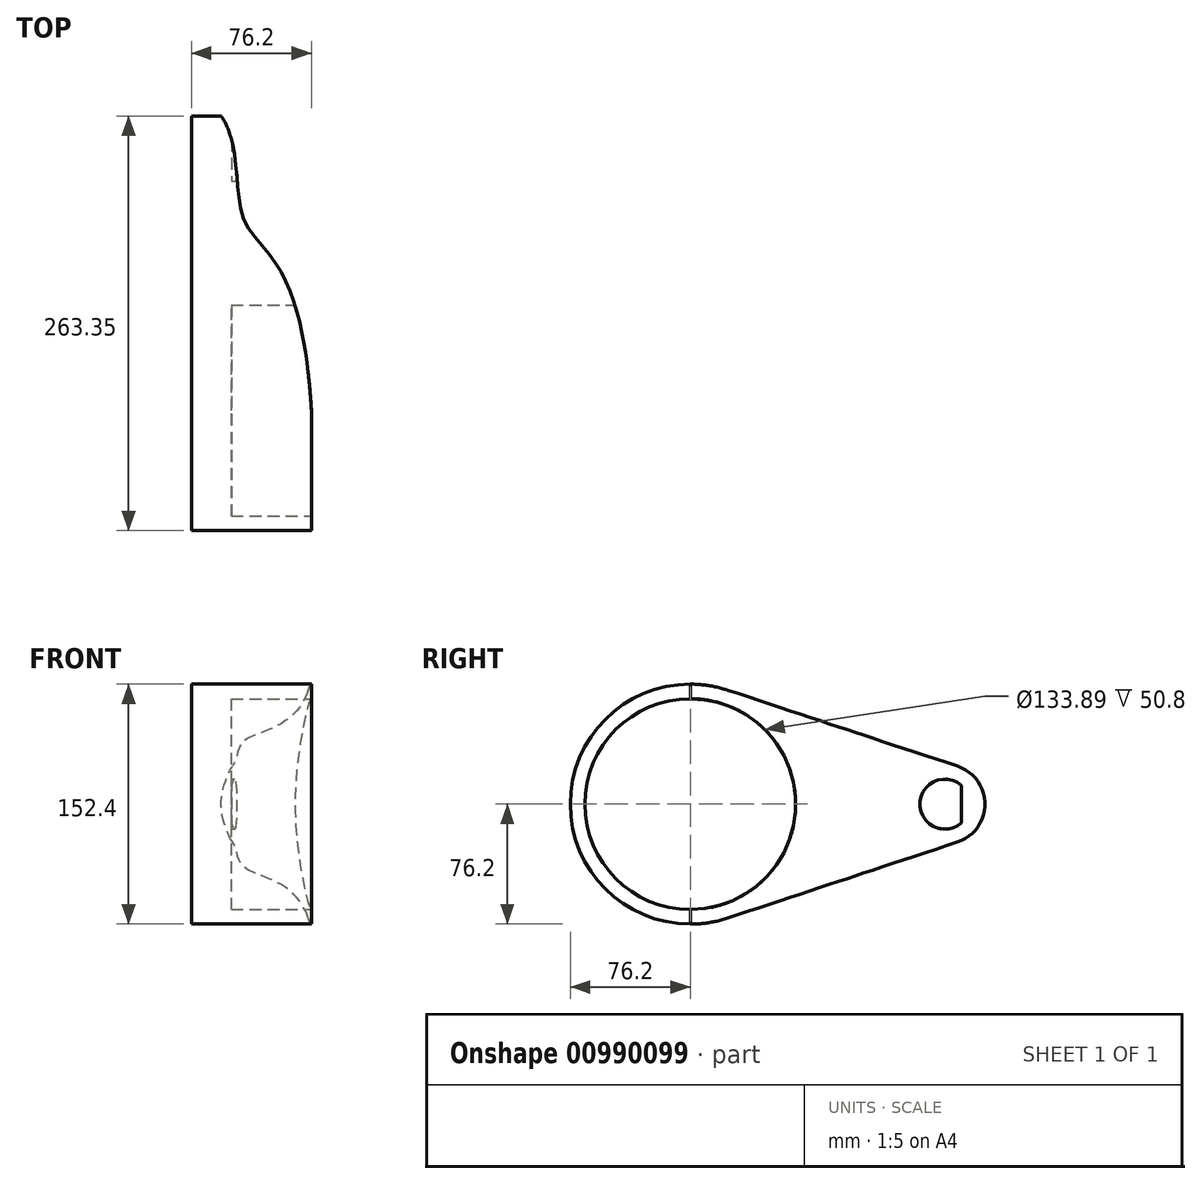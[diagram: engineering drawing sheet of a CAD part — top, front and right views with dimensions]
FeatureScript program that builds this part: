
annotation { "Feature Type Name" : "Feature", "Feature Type Description" : "" }
export const myFeature = defineFeature(function(context is Context, id is Id, definition is map)
    precondition{}
    {
        {
            var Q0;
            Q0=qCreatedBy(makeId("Right.planeOp"),FACE);
            var sketch = newSketch(context, id + "F0", { "sketchPlane" : qUnion([Q0])});
            skArc(sketch, "E0", {"start": v(23.93, 72.34) * mm, "mid": v(-76.2, 0) * mm, "end": v(23.93, -72.34) * mm});
            skArc(sketch, "E1", {"start": v(169.73, -24.11) * mm, "mid": v(187.15, 0) * mm, "end": v(169.73, 24.11) * mm});
            skLineSegment(sketch, "E2", {"start": v(23.93, 72.34) * mm, "end": v(169.73, 24.11) * mm});
            skLineSegment(sketch, "E3", {"start": v(23.93, -72.34) * mm, "end": v(169.73, -24.11) * mm});
            skSolve(sketch);
        }
        {
            var Q0;
            {var subQ0=sQuery(id+"F0.wireOp",EDGE,"E2");Q0=makeQuery(id+"F0.imprint","IMPRINT",FACE,{"disambiguationData":[TD([[makeQuery(id+"F0.imprint","IMPRINT",EDGE,{"derivedFrom":subQ0}),-1.0]])]});}
            var Q1;
            {var subQ0=sQuery(id+"F0.wireOp",EDGE,"E0");var subQ1=makeQuery(id+"F0.imprint","INTERSECT",VERTEX,{"derivedFrom":[subQ0,sQuery(id+"F0.wireOp",EDGE,"E2")]});Q1=makeQuery(id+"F0.imprint","IMPRINT",FACE,{"disambiguationData":[TD([[makeQuery(id+"F0.imprint","IMPRINT",EDGE,{"disambiguationData":[TD([[subQ1,-1.0]])],"derivedFrom":subQ0}),1.0]])]});}
            var Q2;
            {var subQ0=sQuery(id+"F0.wireOp",EDGE,"E1");var subQ1=makeQuery(id+"F0.imprint","INTERSECT",VERTEX,{"derivedFrom":[subQ0,sQuery(id+"F0.wireOp",EDGE,"E2")]});Q2=makeQuery(id+"F0.imprint","IMPRINT",FACE,{"disambiguationData":[TD([[makeQuery(id+"F0.imprint","IMPRINT",EDGE,{"disambiguationData":[TD([[subQ1,-1.0]])],"derivedFrom":subQ0}),1.0]])]});}
            var Q3;
            Q3=qSketchRegion(id+"F2",true);
            extrude(context, id + "F1", {"entities" : qUnion([Q0, Q1, Q2, Q3]), "depth" : 76.2 * mm});
        }
        {
            var Q0;
            Q0=makeQuery(id+"F1.opExtrude","CAP_FACE",FACE,{"disambiguationData":[OSD([sQuery(id+"F0.wireOp",EDGE,"E0"),sQuery(id+"F0.wireOp",EDGE,"E1"),sQuery(id+"F0.wireOp",EDGE,"E2"),sQuery(id+"F0.wireOp",EDGE,"E3")])],"isStart":false});
            var sketch = newSketch(context, id + "F2", { "sketchPlane" : qUnion([Q0])});
            skCircle(sketch, "E4", {"center": v(0, 0) * mm, "radius": 66.94 * mm});
            skCircle(sketch, "E5", {"center": v(161.75, 0) * mm, "radius": 15.88 * mm});
            skSolve(sketch);
        }
        {
            var Q0;
            Q0=makeQuery(id+"F2.imprint","IMPRINT",FACE,{"disambiguationData":[TD([[makeQuery(id+"F2.imprint","IMPRINT",EDGE,{"derivedFrom":sQuery(id+"F2.wireOp",EDGE,"E4")}),1.0]])]});
            var Q1;
            Q1=makeQuery(id+"F2.imprint","IMPRINT",FACE,{"disambiguationData":[TD([[makeQuery(id+"F2.imprint","IMPRINT",EDGE,{"derivedFrom":sQuery(id+"F2.wireOp",EDGE,"E5")}),1.0]])]});
            extrude(context, id + "F3", {"entities" : qUnion([Q0, Q1]), "operationType" : NewBodyOperationType.REMOVE, "oppositeDirection" : true, "depth" : 50.8 * mm});
        }
        {
            var Q0;
            Q0=qCreatedBy(makeId("Top.planeOp"),FACE);
            var sketch = newSketch(context, id + "F4", { "sketchPlane" : qUnion([Q0])});
            skLineSegment(sketch, "E6", {"start": v(76.2, 0) * mm, "end": v(76.2, 199.87) * mm});
            skLineSegment(sketch, "E7", {"start": v(76.2, 199.87) * mm, "end": v(-4.84, 199.87) * mm});
            skFitSpline(sketch, "E8", {"points": [v(76.2, 0) * mm, v(31.76, 126.5) * mm, v(-4.84, 199.87) * mm], "startDerivative": vector(-34.4, 570.06) * mm, "endDerivative": vector(-264.63, 21.07) * mm});
            skSolve(sketch);
        }
        {
            var Q0;
            Q0=makeQuery(id+"F4.imprint","IMPRINT",FACE,{"disambiguationData":[TD([[makeQuery(id+"F4.imprint","IMPRINT",EDGE,{"derivedFrom":sQuery(id+"F4.wireOp",EDGE,"E6")}),1.0]])]});
            extrude(context, id + "F5", {"entities" : qUnion([Q0]), "operationType" : NewBodyOperationType.REMOVE, "endBound" : BoundingType.SYMMETRIC, "oppositeDirection" : true, "depth" : 274.32 * mm, "offsetDistance" : 25.4 * mm});
        }
    });
